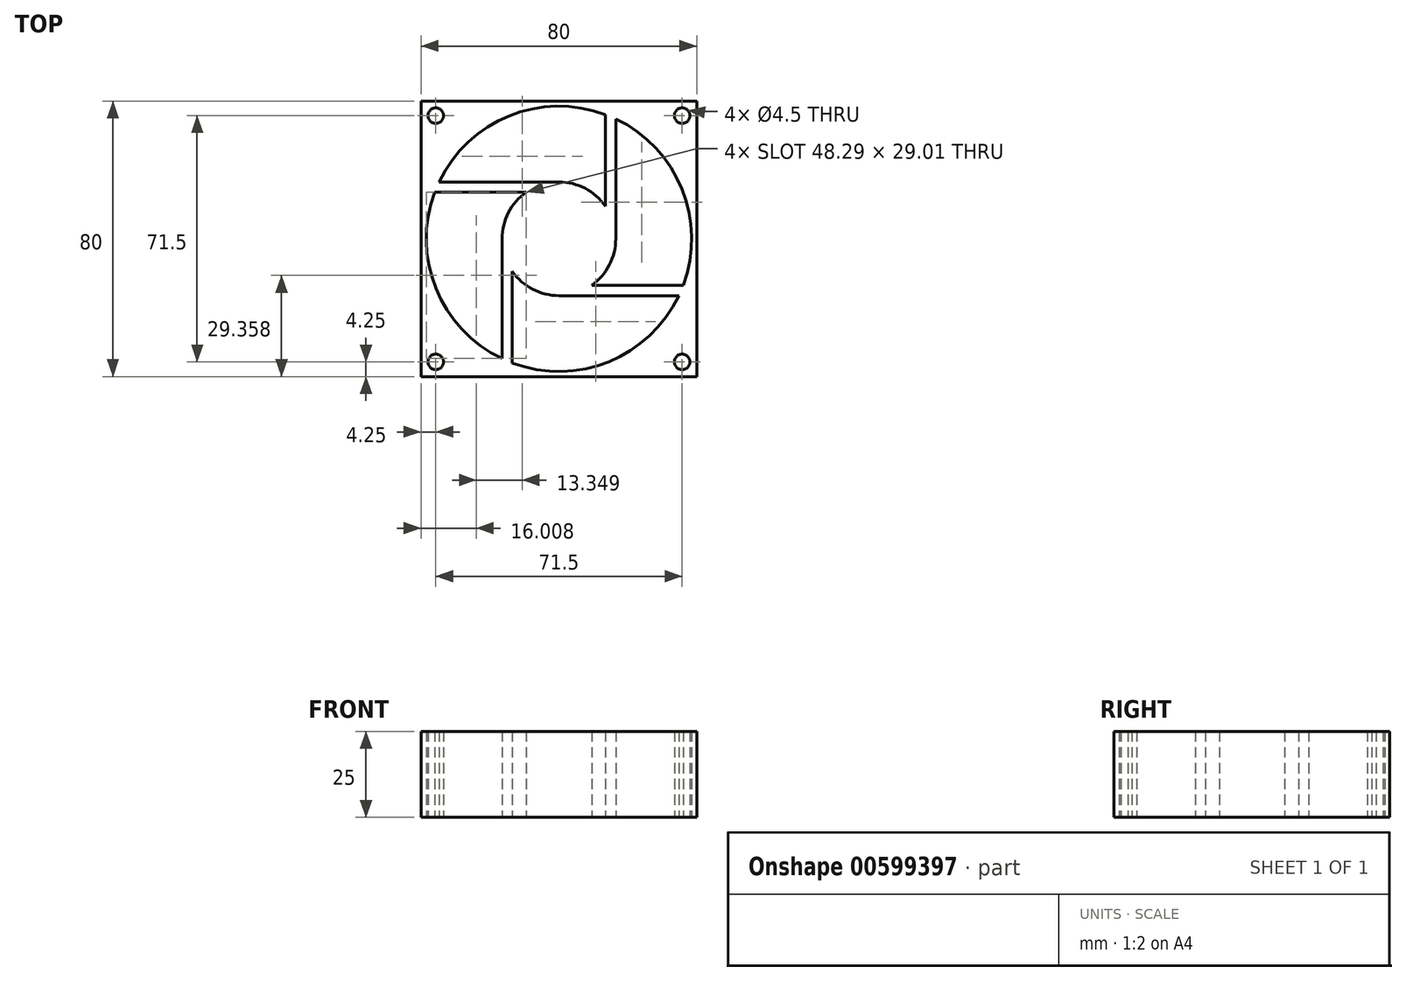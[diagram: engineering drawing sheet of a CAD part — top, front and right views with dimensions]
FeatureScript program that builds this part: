
annotation { "Feature Type Name" : "Feature", "Feature Type Description" : "" }
export const myFeature = defineFeature(function(context is Context, id is Id, definition is map)
    precondition{}
    {
        {
            var Q0;
            Q0=qCreatedBy(makeId("Top.planeOp"),FACE);
            var sketch = newSketch(context, id + "F0", { "sketchPlane" : qUnion([Q0])});
            skLineSegment(sketch, "E0.bottom", {"start": v(-40, 40) * mm, "end": v(40, 40) * mm});
            skLineSegment(sketch, "E0.top", {"start": v(-40, -40) * mm, "end": v(40, -40) * mm});
            skLineSegment(sketch, "E0.left", {"start": v(-40, 40) * mm, "end": v(-40, -40) * mm});
            skLineSegment(sketch, "E0.right", {"start": v(40, 40) * mm, "end": v(40, -40) * mm});
            skLineSegment(sketch, "E1", {"start": v(-40, 40) * mm, "end": v(40, -40) * mm, "construction": true});
            skCircle(sketch, "E2", {"center": v(0, 0) * mm, "radius": 38.5 * mm});
            skLineSegment(sketch, "E3", {"start": v(-40, -40) * mm, "end": v(40, 40) * mm, "construction": true});
            skLineSegment(sketch, "E4.bottom", {"start": v(-35.75, 35.75) * mm, "end": v(35.75, 35.75) * mm, "construction": true});
            skLineSegment(sketch, "E4.top", {"start": v(-35.75, -35.75) * mm, "end": v(35.75, -35.75) * mm, "construction": true});
            skLineSegment(sketch, "E4.left", {"start": v(-35.75, 35.75) * mm, "end": v(-35.75, -35.75) * mm, "construction": true});
            skLineSegment(sketch, "E4.right", {"start": v(35.75, 35.75) * mm, "end": v(35.75, -35.75) * mm, "construction": true});
            skCircle(sketch, "E5", {"center": v(35.75, 35.75) * mm, "radius": 2.25 * mm});
            skCircle(sketch, "E6", {"center": v(-35.75, 35.75) * mm, "radius": 2.25 * mm});
            skCircle(sketch, "E7", {"center": v(-35.75, -35.75) * mm, "radius": 2.25 * mm});
            skCircle(sketch, "E8", {"center": v(35.75, -35.75) * mm, "radius": 2.25 * mm});
            skSolve(sketch);
        }
        {
            var Q0;
            Q0=qSketchRegion(id+"F0",true);
            extrude(context, id + "F1", {"entities" : qUnion([Q0]), "depth" : 25 * mm});
        }
        {
            var Q0;
            Q0=qCreatedBy(makeId("Top.planeOp"),FACE);
            var sketch = newSketch(context, id + "F2", { "sketchPlane" : qUnion([Q0])});
            skCircle(sketch, "E9", {"center": v(0, 0) * mm, "radius": 16.5 * mm});
            skLineSegment(sketch, "E10.bottom", {"start": v(0, 13.5) * mm, "end": v(-36.06, 13.5) * mm});
            skLineSegment(sketch, "E10.top", {"start": v(0, 16.5) * mm, "end": v(-36.06, 16.5) * mm});
            skLineSegment(sketch, "E10.left", {"start": v(0, 13.5) * mm, "end": v(0, 16.5) * mm});
            skLineSegment(sketch, "E10.right", {"start": v(-36.06, 13.5) * mm, "end": v(-36.06, 16.5) * mm});
            skCircle(sketch, "E11.0", {"center": v(0, 0) * mm, "radius": 38.5 * mm});
            skLineSegment(sketch, "E12.1.0", {"start": v(-16.5, 0) * mm, "end": v(-16.5, -36.06) * mm});
            skLineSegment(sketch, "E12.1.1", {"start": v(-13.5, 0) * mm, "end": v(-13.5, -36.06) * mm});
            skLineSegment(sketch, "E12.1.2", {"start": v(-13.5, 0) * mm, "end": v(-16.5, 0) * mm});
            skLineSegment(sketch, "E12.1.3", {"start": v(-13.5, -36.06) * mm, "end": v(-16.5, -36.06) * mm});
            skLineSegment(sketch, "E12.2.0", {"start": v(0, -16.5) * mm, "end": v(36.06, -16.5) * mm});
            skLineSegment(sketch, "E12.2.1", {"start": v(0, -13.5) * mm, "end": v(36.06, -13.5) * mm});
            skLineSegment(sketch, "E12.2.2", {"start": v(0, -13.5) * mm, "end": v(0, -16.5) * mm});
            skLineSegment(sketch, "E12.2.3", {"start": v(36.06, -13.5) * mm, "end": v(36.06, -16.5) * mm});
            skLineSegment(sketch, "E12.3.0", {"start": v(16.5, 0) * mm, "end": v(16.5, 36.06) * mm});
            skLineSegment(sketch, "E12.3.1", {"start": v(13.5, 0) * mm, "end": v(13.5, 36.06) * mm});
            skLineSegment(sketch, "E12.3.2", {"start": v(13.5, 0) * mm, "end": v(16.5, 0) * mm});
            skLineSegment(sketch, "E12.3.3", {"start": v(13.5, 36.06) * mm, "end": v(16.5, 36.06) * mm});
            skSolve(sketch);
        }
        {
            var Q0;
            {var subQ12=sQuery(id+"F2.wireOp",EDGE,"E10.left");Q0=makeQuery(id+"F2.imprint","IMPRINT",FACE,{"disambiguationData":[TD([[makeQuery(id+"F2.imprint","IMPRINT",EDGE,{"derivedFrom":subQ12}),-1.0]])]});}
            var Q1;
            {var subQ0=sQuery(id+"F2.wireOp",EDGE,"E12.3.1");var subQ1=sQuery(id+"F2.wireOp",EDGE,"E9");var subQ2=makeQuery(id+"F2.imprint","INTERSECT",VERTEX,{"derivedFrom":[subQ1,subQ0]});Q1=makeQuery(id+"F2.imprint","IMPRINT",FACE,{"disambiguationData":[TD([[makeQuery(id+"F2.imprint","IMPRINT",EDGE,{"disambiguationData":[TD([[subQ2,1.0]])],"derivedFrom":subQ1}),-1.0]])]});}
            var Q2;
            {var subQ0=sQuery(id+"F2.wireOp",EDGE,"E12.3.2");Q2=makeQuery(id+"F2.imprint","IMPRINT",FACE,{"disambiguationData":[TD([[makeQuery(id+"F2.imprint","IMPRINT",EDGE,{"derivedFrom":subQ0}),1.0]])]});}
            var Q3;
            {var subQ0=sQuery(id+"F2.wireOp",EDGE,"E10.left");Q3=makeQuery(id+"F2.imprint","IMPRINT",FACE,{"disambiguationData":[TD([[makeQuery(id+"F2.imprint","IMPRINT",EDGE,{"derivedFrom":subQ0}),1.0]])]});}
            var Q4;
            {var subQ3=sQuery(id+"F2.wireOp",EDGE,"E10.bottom");var subQ5=sQuery(id+"F2.wireOp",EDGE,"E9");var subQ7=makeQuery(id+"F2.imprint","INTERSECT",VERTEX,{"derivedFrom":[subQ5,subQ3]});Q4=makeQuery(id+"F2.imprint","IMPRINT",FACE,{"disambiguationData":[TD([[makeQuery(id+"F2.imprint","IMPRINT",EDGE,{"disambiguationData":[TD([[subQ7,1.0]])],"derivedFrom":subQ5}),-1.0]])]});}
            var Q5;
            {var subQ0=sQuery(id+"F2.wireOp",EDGE,"E12.1.2");Q5=makeQuery(id+"F2.imprint","IMPRINT",FACE,{"disambiguationData":[TD([[makeQuery(id+"F2.imprint","IMPRINT",EDGE,{"derivedFrom":subQ0}),1.0]])]});}
            var Q6;
            {var subQ0=sQuery(id+"F2.wireOp",EDGE,"E12.1.1");var subQ1=sQuery(id+"F2.wireOp",EDGE,"E9");var subQ2=makeQuery(id+"F2.imprint","INTERSECT",VERTEX,{"derivedFrom":[subQ1,subQ0]});Q6=makeQuery(id+"F2.imprint","IMPRINT",FACE,{"disambiguationData":[TD([[makeQuery(id+"F2.imprint","IMPRINT",EDGE,{"disambiguationData":[TD([[subQ2,1.0]])],"derivedFrom":subQ1}),-1.0]])]});}
            var Q7;
            {var subQ0=sQuery(id+"F2.wireOp",EDGE,"E12.2.2");Q7=makeQuery(id+"F2.imprint","IMPRINT",FACE,{"disambiguationData":[TD([[makeQuery(id+"F2.imprint","IMPRINT",EDGE,{"derivedFrom":subQ0}),1.0]])]});}
            var Q8;
            {var subQ0=sQuery(id+"F2.wireOp",EDGE,"E12.2.1");var subQ1=sQuery(id+"F2.wireOp",EDGE,"E9");var subQ2=makeQuery(id+"F2.imprint","INTERSECT",VERTEX,{"derivedFrom":[subQ1,subQ0]});Q8=makeQuery(id+"F2.imprint","IMPRINT",FACE,{"disambiguationData":[TD([[makeQuery(id+"F2.imprint","IMPRINT",EDGE,{"disambiguationData":[TD([[subQ2,1.0]])],"derivedFrom":subQ1}),-1.0]])]});}
            extrude(context, id + "F3", {"entities" : qUnion([Q0, Q1, Q2, Q3, Q4, Q5, Q6, Q7, Q8]), "operationType" : NewBodyOperationType.ADD, "depth" : 25 * mm});
        }
    });
